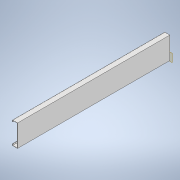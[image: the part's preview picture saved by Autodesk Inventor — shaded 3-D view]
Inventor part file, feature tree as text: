
AUTODESK INVENTOR PART (.ipt)
format: ipt  version: 2020 (Build 240168000, 168)  size: 109,568 bytes
history: native  units: mm
features: other x5, plane x1, extrude x1, sketch x1
ambient origin geometry x8: Origin, YZ Plane, XZ Plane, XY Plane, X Axis, Y Axis, Z Axis, Center Point
bodies: Body1 (feature_tree)
feature tree (8):
  plane  "Work Plane1"
  extrude  "Extrusion2"  Depth=80.0mm
  sketch  "Sketch1"  dims[d2=25.0mm d4=80.0mm d5=25.0mm d6=3.5mm d7=350.0mm d8=2417.4mm d9=0.0mm d10=80.0mm]
  parser-record x1  (decoder bookkeeping rows leaked as tree rows — omitted from the tree; the rows remain in map.json)
  other  "estufa morango 20.iam"
  other  "corners 20feet:1"
  other  "corners bottom:1"
  other  "corner_BL_MIR:1"
note: 1 file-system path scrubbed to <path> (originals preserved in map.json)
